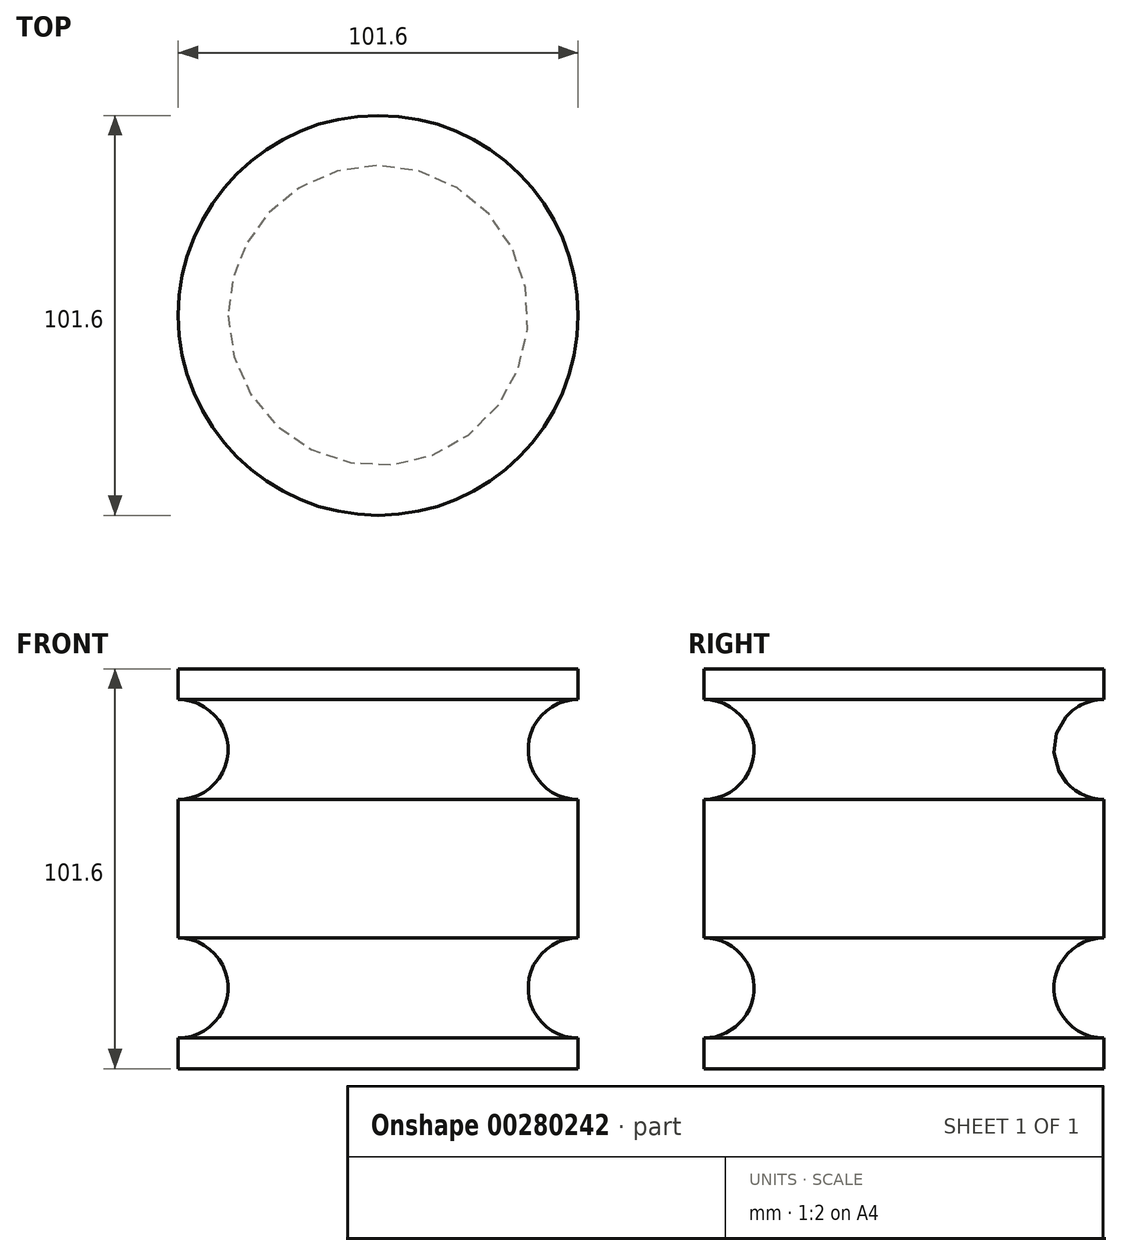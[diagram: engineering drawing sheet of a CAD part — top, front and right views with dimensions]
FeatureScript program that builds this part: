
annotation { "Feature Type Name" : "Feature", "Feature Type Description" : "" }
export const myFeature = defineFeature(function(context is Context, id is Id, definition is map)
    precondition{}
    {
        {
            var Q0;
            Q0=qCreatedBy(makeId("Front.planeOp"),FACE);
            var sketch = newSketch(context, id + "F0", { "sketchPlane" : qUnion([Q0])});
            skLineSegment(sketch, "E0.bottom", {"start": v(0, 0) * mm, "end": v(50.8, 0) * mm});
            skLineSegment(sketch, "E0.top", {"start": v(0, 101.6) * mm, "end": v(50.8, 101.6) * mm});
            skLineSegment(sketch, "E0.left", {"start": v(0, 0) * mm, "end": v(0, 101.6) * mm});
            skLineSegment(sketch, "E0.right", {"start": v(50.8, 0) * mm, "end": v(50.8, 33.2) * mm});
            skArc(sketch, "E1", {"start": v(50.8, 93.8) * mm, "mid": v(38.1, 81.1) * mm, "end": v(50.8, 68.4) * mm});
            skLineSegment(sketch, "E2", {"start": v(50.8, 33.2) * mm, "end": v(50.8, 101.6) * mm});
            skLineSegment(sketch, "E3", {"start": v(63.47, 21.43) * mm, "end": v(63.47, 21.43) * mm});
            skLineSegment(sketch, "E4", {"start": v(50.8, 33.2) * mm, "end": v(50.8, 33.2) * mm});
            skArc(sketch, "E5", {"start": v(50.8, 33.2) * mm, "mid": v(38.1, 20.5) * mm, "end": v(50.8, 7.8) * mm});
            skSolve(sketch);
        }
        {
            var Q0;
            {var subQ1=sQuery(id+"F0.wireOp",EDGE,"E0.bottom");Q0=makeQuery(id+"F0.imprint","IMPRINT",FACE,{"disambiguationData":[TD([[makeQuery(id+"F0.imprint","IMPRINT",EDGE,{"derivedFrom":subQ1}),1.0]])]});}
            var Q1;
            Q1=sQuery(id+"F0.wireOp",EDGE,"E0.left");
            revolve(context, id + "F1", {"entities" : qUnion([Q0]), "axis" : qUnion([Q1]), "revolveType" : RevolveType.FULL});
        }
    });
